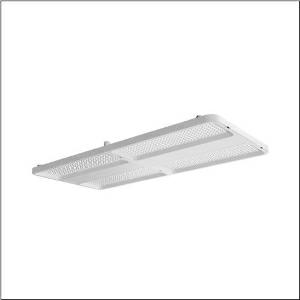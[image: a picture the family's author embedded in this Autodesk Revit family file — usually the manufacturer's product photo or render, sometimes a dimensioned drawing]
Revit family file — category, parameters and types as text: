
# Revit family: highbay_11_maxi_51hn11db4vda
name_source: partatom
category: Lighting Fixtures
units: mm (PartAtom-declared; Revit-internal decimal feet)

## family parameters
Cut with Voids When Loaded = No
Host = Face
Light Source = No
Part Type = Normal
Room Calculation Point = No
Round Connector Dimension = Use Diameter
Shared = No

## types (1)
- --- (1 x LED, 9070 lm, 44.6 W, 4000K)
    Apparent Load = 45 VA
    CIE Flux Codes = 85 97 100 100 100
    Color Rendering = 80
    Color Temperature = 4000K
    Default Elevation = 1800 mm
    Description = high bay luminaire Highbay 11 maxi; direct symmetric narrow distribution, light control with lens of PMMA; UGR ≤ 22 (X = 4H | Y = 8H | S = 0.25H | reflection values 70/50/20); luminous flux: 56.000lm; light colour: 840, colour temperature: 4000K, MacAdam ≤ 2 SDCM (initial), colour rendering: CRI > 80; luminous efficacy: 189,9lm/W; rated service life: 100.000h (L95/B50) at AT= 25°C; control: DALI 2; housing frame of high-performance plastic PA6, matt traffic white (RAL 9016); cover of PMMA; dimension (LxWxH): 946 x 442 x 72mm; luminaire connection: terminal, 5-pole, max. 2.5mm² (cable entry for one cable, Ø 8.5..16mm); mains connection: 230..240V, AC/DC 0/50..60Hz; connected load: 294,9W; protection rating (complete): IP66; insulation class (complete): insulation class I (protective earthing); protection symbol: D; impact resistance: IK08; halogen-free wiring; for central battery installations according to DIN EN 60598-2-22; corresponds to IFS (International Featured Standards) requirements for safety and quality in the food industry; LABS conformity tested according to VDMA 24364:2018-05; certification: CE, ENEC, VDE, UKCA; permissible operating ambient temperature: -40..+50°C (reducing of maximum allowable ambient temperature of 5°C with ceiling mounting); packaging unit: 1 piece; (delivery without accessories; please order mounting accessories separately)
    Height = 72 mm  [stored 0.23622 ft]
    Lamp = 1 x LED
    Lamp Light Flux = 9070 lm
    Lamp Power = 44.6 W
    Lamp count = 1
    Length = 946 mm
    Luminous efficacy = 203 lm/W
    Manufacturer = Siteco
    ModVariant = No
    Model = 51HN11DB4VDA
    Mounting Place = Ceiling
    Mounting Type = Pendant
    Number of Poles = 1
    OnlyDefault = Yes
    Power Factor = 1
    Product Name = Highbay 11 maxi
    Product group = high bay luminaire
    ProductGroupID = 901
    Protection Class = Protection class I
    Protection Degree = IP 66
    RLX_Detail_Level = 1
    RLX_Emergency_Light_Flux = 0 lm
    RLX_Emergency_Type = 0
    RLX_Emergency_Type_DB = No
    RlxData = <blob elided: 22377 chars, md5=2ad99b53>
    Socket = socket
    Standby Power = 0 W
    System Light Flux = 9070 lm
    System Power = 45 W
    Type Comments = : DC mode (central or group accumulator) initial emergency light level
    Type Image = l_1363244.jpg
    URL = http://relux.com
    VarID = @adj_003701
    Voltage = 0 V
    Weight = 0.00 kg
    Width = 442 mm

note: [stored X ft] marks values corroborated as IEEE doubles in the binary element streams (Revit-internal decimal feet)

## geometry (parser evidence)
native form markers: Blend x4, Sweep x10
no freeform markers — native parametric forms only
